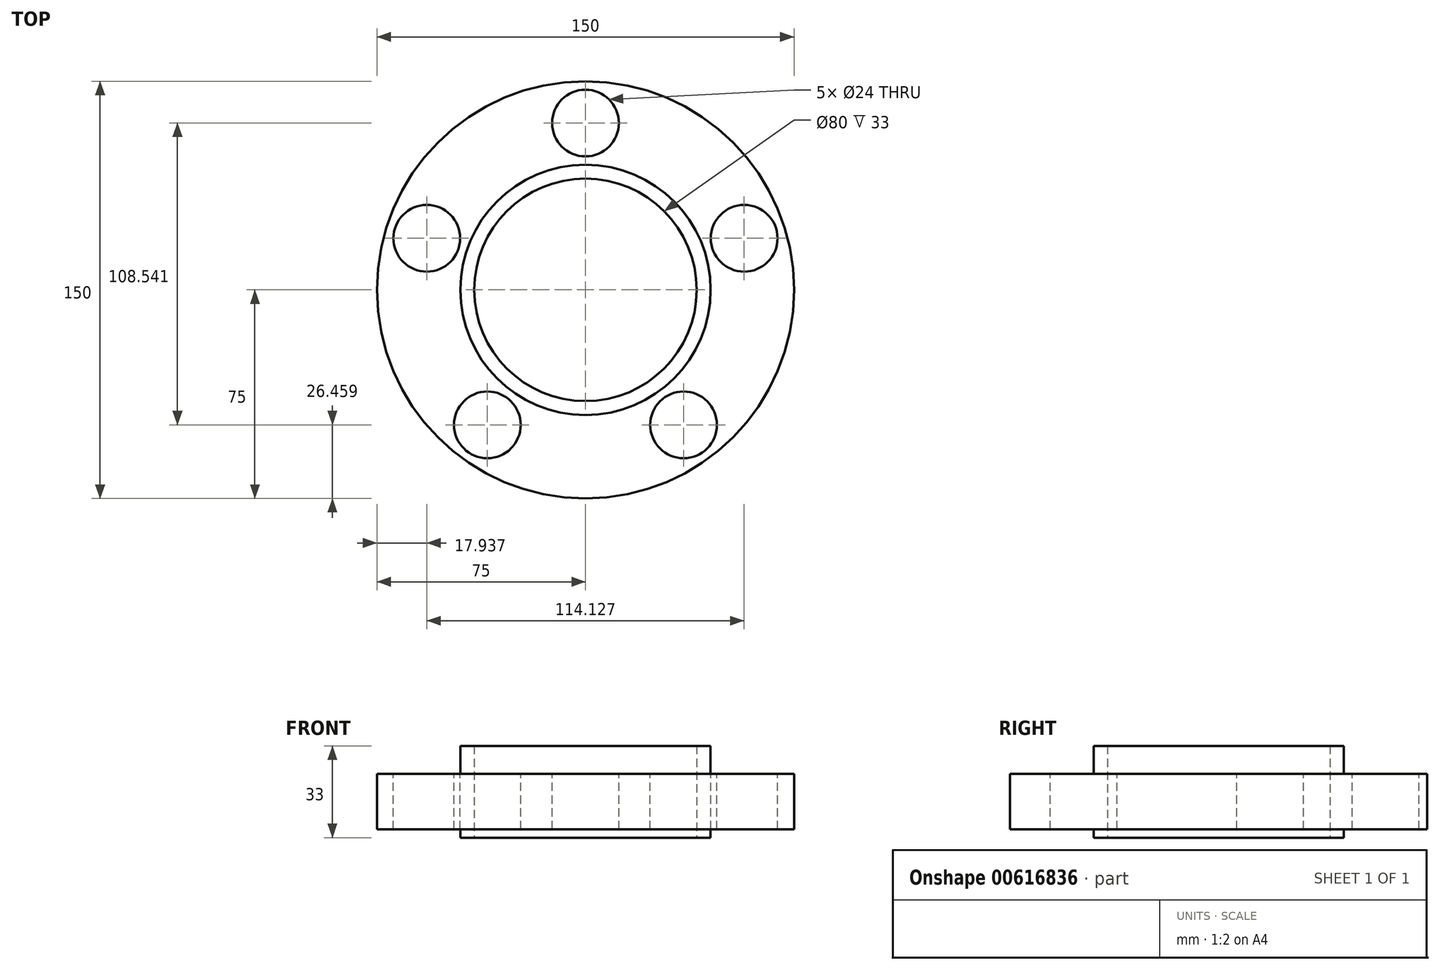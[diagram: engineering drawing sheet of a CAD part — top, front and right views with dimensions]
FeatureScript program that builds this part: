
annotation { "Feature Type Name" : "Feature", "Feature Type Description" : "" }
export const myFeature = defineFeature(function(context is Context, id is Id, definition is map)
    precondition{}
    {
        {
            var Q0;
            Q0=qCreatedBy(makeId("Front.planeOp"),FACE);
            var sketch = newSketch(context, id + "F0", { "sketchPlane" : qUnion([Q0])});
            skLineSegment(sketch, "E0", {"start": v(40, 0) * mm, "end": v(40, 33) * mm});
            skLineSegment(sketch, "E1", {"start": v(40, 33) * mm, "end": v(45, 33) * mm});
            skLineSegment(sketch, "E2", {"start": v(45, 33) * mm, "end": v(45, 23) * mm});
            skLineSegment(sketch, "E3", {"start": v(45, 23) * mm, "end": v(75, 23) * mm});
            skLineSegment(sketch, "E4", {"start": v(75, 23) * mm, "end": v(75, 3) * mm});
            skLineSegment(sketch, "E5", {"start": v(75, 3) * mm, "end": v(45, 3) * mm});
            skLineSegment(sketch, "E6", {"start": v(45, 3) * mm, "end": v(45, 0) * mm});
            skLineSegment(sketch, "E7", {"start": v(45, 0) * mm, "end": v(40, 0) * mm});
            skLineSegment(sketch, "E8", {"start": v(0, 0) * mm, "end": v(0, 79.57) * mm, "construction": true});
            skSolve(sketch);
        }
        {
            var Q0;
            Q0=makeQuery(id+"F0.imprint","IMPRINT",FACE,{"disambiguationData":[TD([[makeQuery(id+"F0.imprint","IMPRINT",EDGE,{"derivedFrom":sQuery(id+"F0.wireOp",EDGE,"E0")}),-1.0]])]});
            var Q1;
            Q1=sQuery(id+"F0.wireOp",EDGE,"E8");
            revolve(context, id + "F1", {"surfaceOperationType" : NewSurfaceOperationType.NEW, "entities" : qUnion([Q0]), "axis" : qUnion([Q1]), "revolveType" : RevolveType.FULL});
        }
        {
            var Q0;
            Q0=makeQuery(id+"F1.opRevolve","SWEPT_FACE",FACE,{"disambiguationData":[OSD([sQuery(id+"F0.wireOp",EDGE,"E3")])]});
            var sketch = newSketch(context, id + "F2", { "sketchPlane" : qUnion([Q0])});
            skCircle(sketch, "E9", {"center": v(0, 0) * mm, "radius": 60 * mm, "construction": true});
            skCircle(sketch, "E10", {"center": v(0, 60) * mm, "radius": 12 * mm});
            skCircle(sketch, "E11.1.0", {"center": v(-57.06, 18.54) * mm, "radius": 12 * mm});
            skCircle(sketch, "E11.2.0", {"center": v(-35.27, -48.54) * mm, "radius": 12 * mm});
            skCircle(sketch, "E11.3.0", {"center": v(35.27, -48.54) * mm, "radius": 12 * mm});
            skCircle(sketch, "E11.4.0", {"center": v(57.06, 18.54) * mm, "radius": 12 * mm});
            skSolve(sketch);
        }
        {
            var Q0;
            Q0=qSketchRegion(id+"F2",true);
            extrude(context, id + "F3", {"entities" : qUnion([Q0]), "operationType" : NewBodyOperationType.REMOVE, "endBound" : BoundingType.UP_TO_NEXT, "oppositeDirection" : true, "depth" : 25 * mm, "offsetDistance" : 25 * mm});
        }
    });
